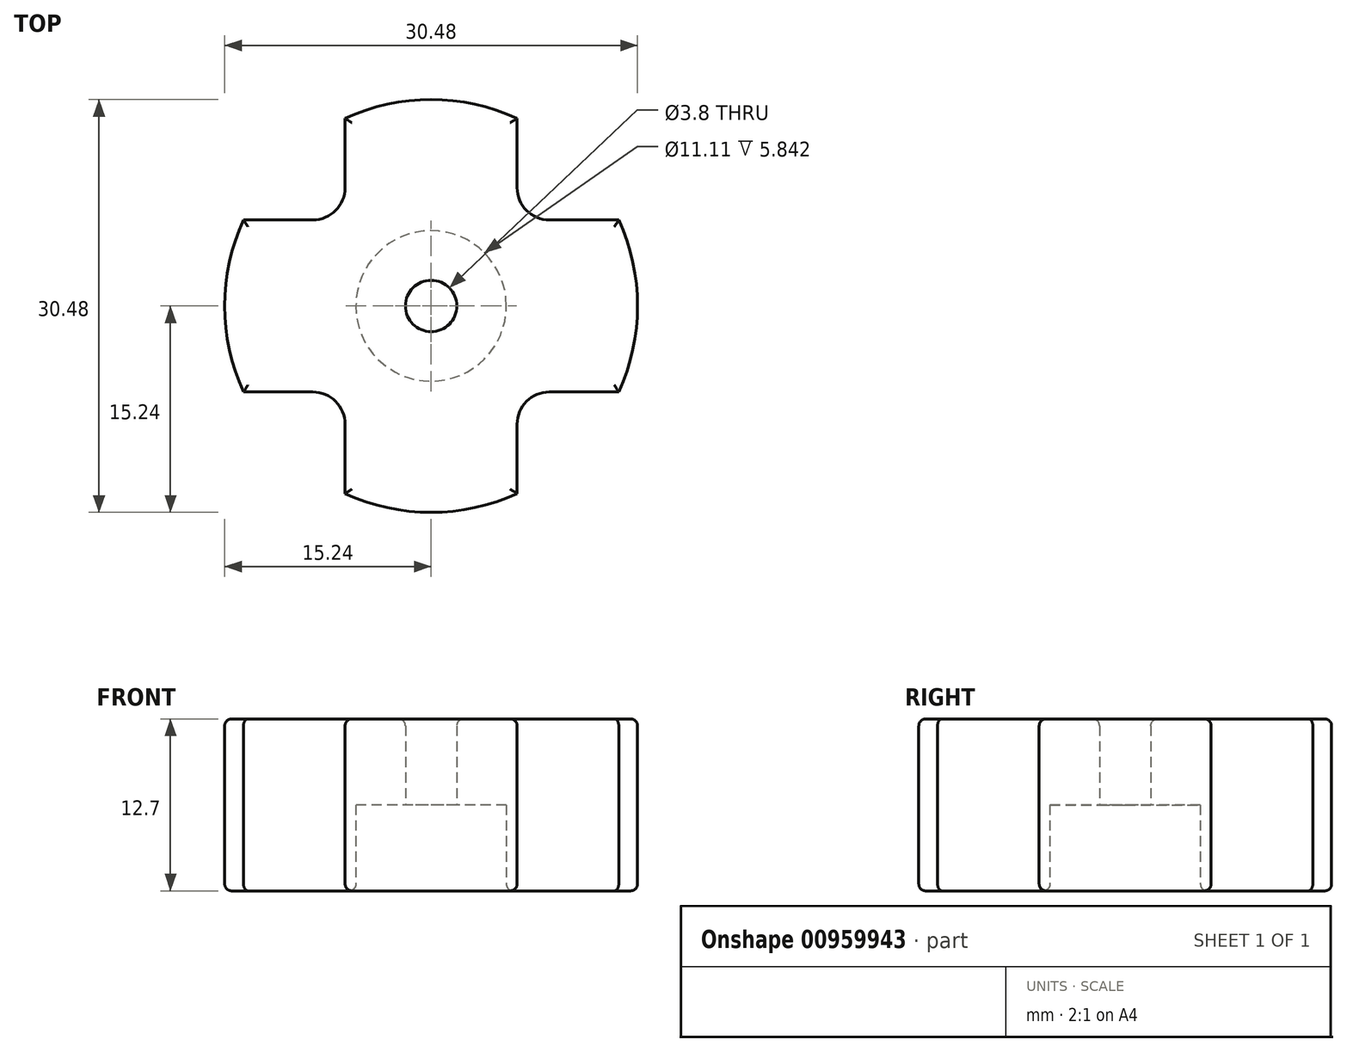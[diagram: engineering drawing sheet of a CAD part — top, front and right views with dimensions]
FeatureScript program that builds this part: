
annotation { "Feature Type Name" : "Feature", "Feature Type Description" : "" }
export const myFeature = defineFeature(function(context is Context, id is Id, definition is map)
    precondition{}
    {
        {
            var Q0;
            Q0=qCreatedBy(makeId("Top.planeOp"),FACE);
            var sketch = newSketch(context, id + "F0", { "sketchPlane" : qUnion([Q0])});
            skCircle(sketch, "E0", {"center": v(0, 0) * mm, "radius": 15.24 * mm});
            skLineSegment(sketch, "E1", {"start": v(0, -15.24) * mm, "end": v(0, 20.54) * mm, "construction": true});
            skLineSegment(sketch, "E2", {"start": v(-19.18, 0) * mm, "end": v(20.27, 0) * mm, "construction": true});
            skLineSegment(sketch, "E3", {"start": v(-19.18, -6.35) * mm, "end": v(19.34, -6.35) * mm, "construction": true});
            skLineSegment(sketch, "E4", {"start": v(-6.35, -19) * mm, "end": v(-6.35, 22) * mm, "construction": true});
            skLineSegment(sketch, "E5.MirrorCS", {"start": v(6.35, -19) * mm, "end": v(6.35, 22) * mm, "construction": true});
            skLineSegment(sketch, "E6.MirrorCS", {"start": v(-19.18, 6.35) * mm, "end": v(19.34, 6.35) * mm, "construction": true});
            skLineSegment(sketch, "E7", {"start": v(-19.18, -6.35) * mm, "end": v(-6.35, -6.35) * mm});
            skLineSegment(sketch, "E8", {"start": v(-6.35, -6.35) * mm, "end": v(-6.35, -19) * mm});
            skLineSegment(sketch, "E9.MirrorCS", {"start": v(6.35, -6.35) * mm, "end": v(6.35, -19) * mm});
            skLineSegment(sketch, "E10.MirrorCS", {"start": v(19.18, -6.35) * mm, "end": v(6.35, -6.35) * mm});
            skLineSegment(sketch, "E11.MirrorCS", {"start": v(-19.18, 6.35) * mm, "end": v(-6.35, 6.35) * mm});
            skLineSegment(sketch, "E12.MirrorCS", {"start": v(-6.35, 6.35) * mm, "end": v(-6.35, 19) * mm});
            skLineSegment(sketch, "E13.MirrorCS", {"start": v(6.35, 6.35) * mm, "end": v(6.35, 19) * mm});
            skLineSegment(sketch, "E14.MirrorCS", {"start": v(19.18, 6.35) * mm, "end": v(6.35, 6.35) * mm});
            skCircle(sketch, "E15", {"center": v(0, 0) * mm, "radius": 5.56 * mm});
            skSolve(sketch);
        }
        {
            var Q0;
            Q0=makeQuery(id+"F0.imprint","IMPRINT",FACE,{"disambiguationData":[TD([[makeQuery(id+"F0.imprint","IMPRINT",EDGE,{"derivedFrom":sQuery(id+"F0.wireOp",EDGE,"E15")}),-1.0]])]});
            var Q1;
            Q1=makeQuery(id+"F0.imprint","IMPRINT",FACE,{"disambiguationData":[TD([[makeQuery(id+"F0.imprint","IMPRINT",EDGE,{"derivedFrom":sQuery(id+"F0.wireOp",EDGE,"E15")}),1.0]])]});
            extrude(context, id + "F1", {"entities" : qUnion([Q0, Q1]), "depth" : 12.7 * mm, "offsetDistance" : 25.4 * mm});
        }
        {
            var Q0;
            Q0=sQuery(id+"F0.wireOp",VERTEX,"E0.center");
            var Q1;
            Q1=makeQuery(id+"F1.opExtrude","SWEPT_BODY",BODY,{"disambiguationData":[OSD([sQuery(id+"F0.wireOp",EDGE,"E0")])]});
            hole(context, id + "F2", {"style" : HoleStyle.SIMPLE, "endStyle" : HoleEndStyle.THROUGH, "oppositeDirection" : true, "standardTappedOrClearance" : lookupTablePath({ "standard" : "ANSI", "engagement" : "75%", "pitch" : "24 tpi", "size" : "#10", "type" : "Tapped" }), "standardBlindInLast" : lookupTablePath({ "standard" : "ANSI", "fit" : "Normal", "engagement" : "75%", "pitch" : "24 tpi", "size" : "#10", "type" : "Clearance & tapped" }), "holeDiameter" : 3.8 * mm, "majorDiameter" : 4.83 * mm, "showTappedDepth" : true, "isTappedThrough" : true, "tappedDepth" : 11.76 * mm, "tapClearance" : 3, "locations" : qUnion([Q0]), "scope" : qUnion([Q1])});
        }
        {
            var Q0;
            Q0=makeQuery(id+"F0.imprint","IMPRINT",FACE,{"disambiguationData":[TD([[makeQuery(id+"F0.imprint","IMPRINT",EDGE,{"derivedFrom":sQuery(id+"F0.wireOp",EDGE,"E15")}),1.0]])]});
            extrude(context, id + "F3", {"entities" : qUnion([Q0]), "operationType" : NewBodyOperationType.REMOVE, "depth" : 6.35 * mm, "offsetDistance" : 25.4 * mm});
        }
        {
            var Q0;
            Q0=makeQuery(id+"F1.opExtrude","SWEPT_EDGE",EDGE,{"disambiguationData":[OSD([sQuery(id+"F0.wireOp",EDGE,"E7"),sQuery(id+"F0.wireOp",EDGE,"E8")])]});
            var Q1;
            Q1=makeQuery(id+"F1.opExtrude","SWEPT_EDGE",EDGE,{"disambiguationData":[OSD([sQuery(id+"F0.wireOp",EDGE,"E11.MirrorCS"),sQuery(id+"F0.wireOp",EDGE,"E12.MirrorCS")])]});
            var Q2;
            Q2=makeQuery(id+"F1.opExtrude","SWEPT_EDGE",EDGE,{"disambiguationData":[OSD([sQuery(id+"F0.wireOp",EDGE,"E13.MirrorCS"),sQuery(id+"F0.wireOp",EDGE,"E14.MirrorCS")])]});
            var Q3;
            Q3=makeQuery(id+"F1.opExtrude","SWEPT_EDGE",EDGE,{"disambiguationData":[OSD([sQuery(id+"F0.wireOp",EDGE,"E9.MirrorCS"),sQuery(id+"F0.wireOp",EDGE,"E10.MirrorCS")])]});
            fillet(context, id + "F4", {"entities" : qUnion([Q0, Q1, Q2, Q3]), "radius" : 2.38 * mm, "tangentPropagation" : true, "allowEdgeOverflow" : false});
        }
        {
            var Q0;
            Q0=makeQuery(id+"F1.opExtrude","CAP_FACE",FACE,{"disambiguationData":[OSD([sQuery(id+"F0.wireOp",EDGE,"E0")])],"isStart":true});
            var Q1;
            Q1=makeQuery(id+"F1.opExtrude","CAP_FACE",FACE,{"disambiguationData":[OSD([sQuery(id+"F0.wireOp",EDGE,"E0")])],"isStart":false});
            var Q2;
            Q2=makeQuery(id+"FlHHysuArryxnE7_1.hole-0.boolean.opBoolean","INTERSECT",EDGE,{"derivedFrom":[makeQuery(id+"F2.hole-0.boolean.opBoolean","COPY",FACE,{"derivedFrom":makeQuery(id+"F2.hole-0.opRevolve","SWEPT_FACE",FACE,{"disambiguationData":[OSD([sQuery(id+"F2.hole-0.sketch.wireOp",EDGE,"core_line_2")])]})}),makeQuery(id+"FlHHysuArryxnE7_1.hole-0.opRevolve","SWEPT_FACE",FACE,{"disambiguationData":[OSD([sQuery(id+"FlHHysuArryxnE7_1.hole-0.sketch.wireOp",EDGE,"core_line_1")])]})]});
            fillet(context, id + "F5", {"entities" : qUnion([Q0, Q1, Q2]), "radius" : 0.5 * mm, "tangentPropagation" : true, "allowEdgeOverflow" : false});
        }
    });
